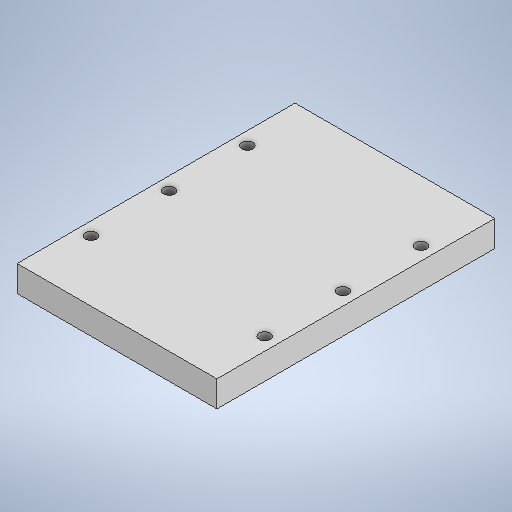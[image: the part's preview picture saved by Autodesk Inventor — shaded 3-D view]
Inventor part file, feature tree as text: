
AUTODESK INVENTOR PART (.ipt)
format: ipt  version: 2025 (Build 290162010, 162A)  size: 239,104 bytes
history: native  units: in
note: dims shown in document units (in); Inventor stores cm internally (conversion verified against a paired STEP export)
features: extrude x2, sketch x2
ambient origin geometry x8: Origin, YZ Plane, XZ Plane, XY Plane, X Axis, Y Axis, Z Axis, Center Point
bodies: Solid1 (feature_tree)
feature tree (4):
  extrude  "Extrusion1"  Depth=8.0in
  extrude  "Extrusion2"  Depth=0.75in
  sketch  "Sketch1"  dims[d0=5.75in d1=8.0in]
  sketch  "Sketch2"  dims[d2=0.75in d3=0.0in d4=0.322in d5=0.322in d6=0.322in d7=0.322in d8=0.322in d9=0.322in d10=1.75in d11=4.0in d12=6.25in d13=1.75in d14=4.0in d15=6.25in d16=0.375in d17=0.375in d18=0.375in d19=0.375in d20=0.375in d21=0.375in d22=0.75in d23=0.0in]
